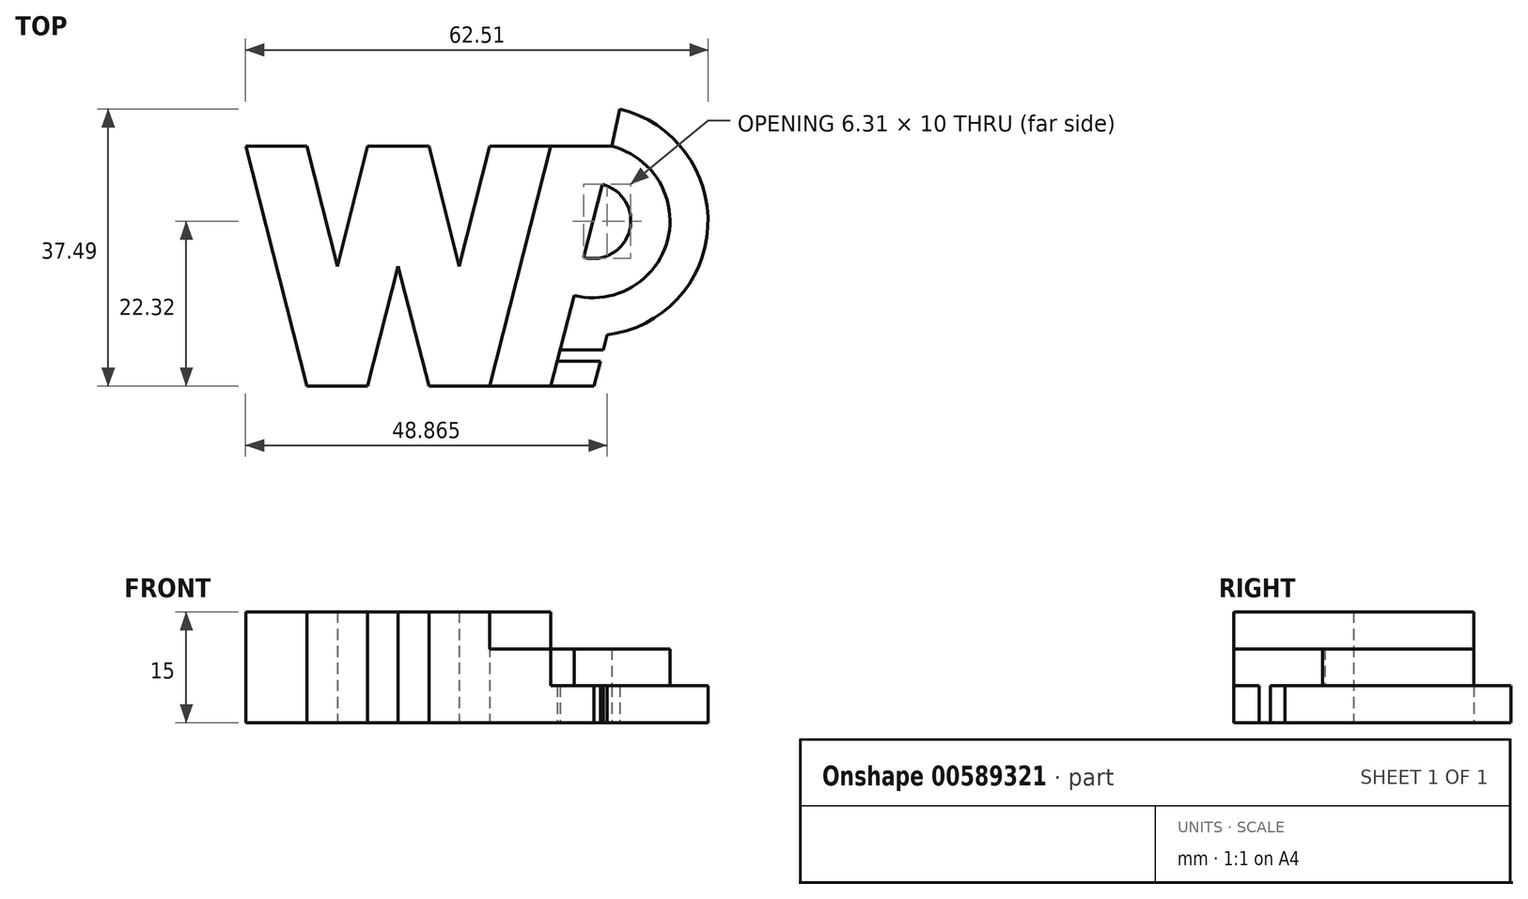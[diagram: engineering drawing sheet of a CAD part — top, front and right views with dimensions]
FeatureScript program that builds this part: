
annotation { "Feature Type Name" : "Feature", "Feature Type Description" : "" }
export const myFeature = defineFeature(function(context is Context, id is Id, definition is map)
    precondition{}
    {
        {
            var Q0;
            Q0=qCreatedBy(makeId("Top.planeOp"),FACE);
            var sketch = newSketch(context, id + "F0", { "sketchPlane" : qUnion([Q0])});
            skLineSegment(sketch, "E0", {"start": v(-45.97, 22) * mm, "end": v(-37.71, -10.45) * mm});
            skLineSegment(sketch, "E1", {"start": v(-37.71, -10.45) * mm, "end": v(-29.46, -10.45) * mm});
            skLineSegment(sketch, "E2", {"start": v(-29.46, -10.45) * mm, "end": v(-25.33, 5.77) * mm});
            skLineSegment(sketch, "E3", {"start": v(-25.33, 5.77) * mm, "end": v(-21.2, -10.45) * mm});
            skLineSegment(sketch, "E4", {"start": v(-21.2, -10.45) * mm, "end": v(-12.95, -10.45) * mm});
            skLineSegment(sketch, "E5", {"start": v(-12.95, -10.45) * mm, "end": v(-4.7, 22) * mm});
            skLineSegment(sketch, "E6", {"start": v(-4.7, 22) * mm, "end": v(-12.95, 22) * mm});
            skLineSegment(sketch, "E7", {"start": v(-12.95, 22) * mm, "end": v(-17.08, 5.77) * mm});
            skLineSegment(sketch, "E8", {"start": v(-17.08, 5.77) * mm, "end": v(-21.2, 22) * mm});
            skLineSegment(sketch, "E9", {"start": v(-21.2, 22) * mm, "end": v(-29.46, 22) * mm});
            skLineSegment(sketch, "E10", {"start": v(-29.46, 22) * mm, "end": v(-33.59, 5.77) * mm});
            skLineSegment(sketch, "E11", {"start": v(-33.59, 5.77) * mm, "end": v(-37.71, 22) * mm});
            skLineSegment(sketch, "E12", {"start": v(-37.71, 22) * mm, "end": v(-45.97, 22) * mm});
            skLineSegment(sketch, "E13", {"start": v(-12.95, -10.45) * mm, "end": v(-4.7, -10.45) * mm});
            skLineSegment(sketch, "E14", {"start": v(-4.7, -10.45) * mm, "end": v(-1.57, 1.85) * mm});
            skLineSegment(sketch, "E15", {"start": v(-1.57, 1.85) * mm, "end": v(3.56, 22) * mm, "construction": true});
            skLineSegment(sketch, "E16", {"start": v(-0.28, 6.92) * mm, "end": v(2.27, 16.92) * mm});
            skLineSegment(sketch, "E17", {"start": v(-4.7, 22) * mm, "end": v(3.56, 22) * mm});
            skLineSegment(sketch, "E18", {"start": v(3.56, 22) * mm, "end": v(4.6, 27.07) * mm});
            skArc(sketch, "E19", {"start": v(-0.26, 6.97) * mm, "mid": v(5.95, 10.66) * mm, "end": v(2.26, 16.87) * mm});
            skArc(sketch, "E20", {"start": v(-1.56, 1.85) * mm, "mid": v(11.07, 9.36) * mm, "end": v(3.56, 22) * mm});
            skArc(sketch, "E21", {"start": v(2.88, -3.5) * mm, "mid": v(16.51, 11.05) * mm, "end": v(4.6, 27.04) * mm});
            skLineSegment(sketch, "E22", {"start": v(-4.7, -10.45) * mm, "end": v(1.12, -10.45) * mm});
            skLineSegment(sketch, "E23", {"start": v(1.12, -10.45) * mm, "end": v(1.98, -7.04) * mm});
            skLineSegment(sketch, "E24", {"start": v(-3.83, -7.04) * mm, "end": v(1.98, -7.04) * mm});
            skLineSegment(sketch, "E25", {"start": v(2.37, -5.51) * mm, "end": v(-3.44, -5.51) * mm});
            skLineSegment(sketch, "E26.trimOffspring", {"start": v(2.37, -5.51) * mm, "end": v(2.88, -3.5) * mm});
            skLineSegment(sketch, "E27", {"start": v(-1.56, 1.85) * mm, "end": v(-3.44, -5.51) * mm});
            skLineSegment(sketch, "E28", {"start": v(-3.83, -7.04) * mm, "end": v(-4.7, -10.45) * mm});
            skSolve(sketch);
        }
        {
            var Q0;
            Q0=makeQuery(id+"F0.imprint","IMPRINT",FACE,{"disambiguationData":[TD([[makeQuery(id+"F0.imprint","IMPRINT",EDGE,{"derivedFrom":sQuery(id+"F0.wireOp",EDGE,"E0")}),1.0]])]});
            extrude(context, id + "F1", {"entities" : qUnion([Q0]), "depth" : 15 * mm, "offsetDistance" : 25 * mm});
        }
        {
            var Q0;
            {var subQ3=sQuery(id+"F0.wireOp",EDGE,"E5");Q0=makeQuery(id+"F0.imprint","IMPRINT",FACE,{"disambiguationData":[TD([[makeQuery(id+"F0.imprint","IMPRINT",EDGE,{"derivedFrom":subQ3}),-1.0]])]});}
            extrude(context, id + "F2", {"entities" : qUnion([Q0]), "operationType" : NewBodyOperationType.ADD, "depth" : 10 * mm, "offsetDistance" : 25 * mm});
        }
        {
            var Q0;
            {var subQ1=sQuery(id+"F0.wireOp",EDGE,"E20");Q0=makeQuery(id+"F0.imprint","IMPRINT",FACE,{"disambiguationData":[TD([[makeQuery(id+"F0.imprint","IMPRINT",EDGE,{"derivedFrom":subQ1}),-1.0]])]});}
            var Q1;
            Q1=makeQuery(id+"F0.imprint","IMPRINT",FACE,{"disambiguationData":[TD([[makeQuery(id+"F0.imprint","IMPRINT",EDGE,{"derivedFrom":sQuery(id+"F0.wireOp",EDGE,"E22")}),1.0]])]});
            extrude(context, id + "F3", {"entities" : qUnion([Q0, Q1]), "operationType" : NewBodyOperationType.ADD, "depth" : 5 * mm, "offsetDistance" : 25 * mm});
        }
    });
